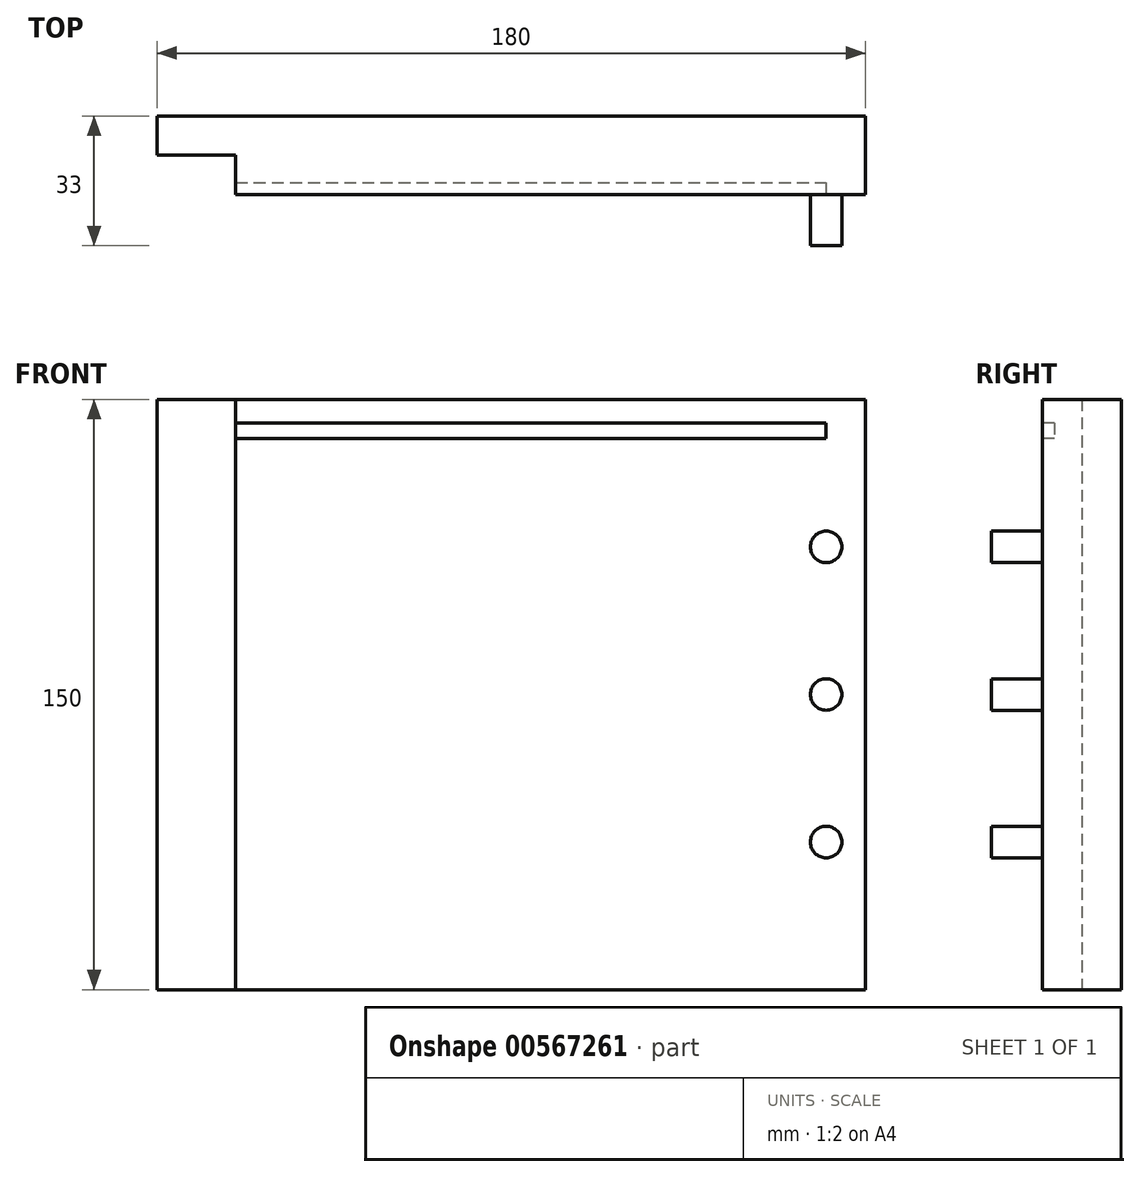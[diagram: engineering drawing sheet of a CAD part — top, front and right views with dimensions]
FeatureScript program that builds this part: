
annotation { "Feature Type Name" : "Feature", "Feature Type Description" : "" }
export const myFeature = defineFeature(function(context is Context, id is Id, definition is map)
    precondition{}
    {
        {
            var Q0;
            Q0=qCreatedBy(makeId("Front.planeOp"),FACE);
            var sketch = newSketch(context, id + "F0", { "sketchPlane" : qUnion([Q0])});
            skLineSegment(sketch, "E0.bottom", {"start": v(-86.18, 94.94) * mm, "end": v(93.82, 94.94) * mm});
            skLineSegment(sketch, "E0.top", {"start": v(-86.18, -55.06) * mm, "end": v(93.82, -55.06) * mm});
            skLineSegment(sketch, "E0.left", {"start": v(-86.18, 94.94) * mm, "end": v(-86.18, -55.06) * mm});
            skLineSegment(sketch, "E0.right", {"start": v(93.82, 94.94) * mm, "end": v(93.82, -55.06) * mm});
            skSolve(sketch);
        }
        {
            var Q0;
            Q0=makeQuery(id+"F0.imprint","IMPRINT",FACE,{"disambiguationData":[TD([[makeQuery(id+"F0.imprint","IMPRINT",EDGE,{"derivedFrom":sQuery(id+"F0.wireOp",EDGE,"E0.bottom")}),-1.0]])]});
            extrude(context, id + "F1", {"entities" : qUnion([Q0]), "depth" : 20 * mm, "offsetDistance" : 25 * mm});
        }
        {
            var Q0;
            Q0=makeQuery(id+"F1.opExtrude","CAP_FACE",FACE,{"disambiguationData":[OSD([sQuery(id+"F0.wireOp",EDGE,"E0.bottom"),sQuery(id+"F0.wireOp",EDGE,"E0.top"),sQuery(id+"F0.wireOp",EDGE,"E0.left"),sQuery(id+"F0.wireOp",EDGE,"E0.right")])],"isStart":false});
            var sketch = newSketch(context, id + "F2", { "sketchPlane" : qUnion([Q0])});
            skLineSegment(sketch, "E1", {"start": v(-66.18, 94.94) * mm, "end": v(-66.18, -55.06) * mm});
            skSolve(sketch);
        }
        {
            var Q0;
            {var subQ0=sQuery(id+"F2.wireOp",EDGE,"E1");Q0=makeQuery(id+"F2.imprint","IMPRINT",FACE,{"disambiguationData":[TD([[makeQuery(id+"F2.imprint","IMPRINT",EDGE,{"derivedFrom":subQ0}),-1.0]])]});}
            extrude(context, id + "F3", {"entities" : qUnion([Q0]), "operationType" : NewBodyOperationType.REMOVE, "oppositeDirection" : true, "depth" : 10 * mm, "offsetDistance" : 25 * mm});
        }
        {
            var Q0;
            Q0=makeQuery(id+"F1.opExtrude","CAP_FACE",FACE,{"disambiguationData":[OSD([sQuery(id+"F0.wireOp",EDGE,"E0.bottom"),sQuery(id+"F0.wireOp",EDGE,"E0.top"),sQuery(id+"F0.wireOp",EDGE,"E0.left"),sQuery(id+"F0.wireOp",EDGE,"E0.right")])],"isStart":false});
            var sketch = newSketch(context, id + "F4", { "sketchPlane" : qUnion([Q0])});
            skCircle(sketch, "E2", {"center": v(83.82, 57.44) * mm, "radius": 4 * mm});
            skLineSegment(sketch, "E3", {"start": v(73.82, 94.94) * mm, "end": v(73.82, -55.06) * mm});
            skCircle(sketch, "E4", {"center": v(83.82, -17.56) * mm, "radius": 4 * mm});
            skCircle(sketch, "E5", {"center": v(83.82, 19.94) * mm, "radius": 4 * mm});
            skSolve(sketch);
        }
        {
            var Q0;
            Q0=makeQuery(id+"F4.imprint","IMPRINT",FACE,{"disambiguationData":[TD([[makeQuery(id+"F4.imprint","IMPRINT",EDGE,{"derivedFrom":sQuery(id+"F4.wireOp",EDGE,"E2")}),1.0]])]});
            var Q1;
            Q1=makeQuery(id+"F4.imprint","IMPRINT",FACE,{"disambiguationData":[TD([[makeQuery(id+"F4.imprint","IMPRINT",EDGE,{"derivedFrom":sQuery(id+"F4.wireOp",EDGE,"E5")}),1.0]])]});
            var Q2;
            Q2=makeQuery(id+"F4.imprint","IMPRINT",FACE,{"disambiguationData":[TD([[makeQuery(id+"F4.imprint","IMPRINT",EDGE,{"derivedFrom":sQuery(id+"F4.wireOp",EDGE,"E4")}),1.0]])]});
            extrude(context, id + "F5", {"entities" : qUnion([Q0, Q1, Q2]), "operationType" : NewBodyOperationType.ADD, "depth" : 13 * mm, "offsetDistance" : 25 * mm});
        }
        {
            var Q0;
            Q0=makeQuery(id+"F1.opExtrude","CAP_FACE",FACE,{"disambiguationData":[OSD([sQuery(id+"F0.wireOp",EDGE,"E0.bottom"),sQuery(id+"F0.wireOp",EDGE,"E0.top"),sQuery(id+"F0.wireOp",EDGE,"E0.left"),sQuery(id+"F0.wireOp",EDGE,"E0.right")])],"isStart":false});
            var sketch = newSketch(context, id + "F6", { "sketchPlane" : qUnion([Q0])});
            skLineSegment(sketch, "E6", {"start": v(-66.18, 84.94) * mm, "end": v(-66.18, 88.94) * mm});
            skLineSegment(sketch, "E7", {"start": v(-66.18, 88.94) * mm, "end": v(83.82, 88.94) * mm});
            skLineSegment(sketch, "E8", {"start": v(-66.18, 84.94) * mm, "end": v(83.82, 84.94) * mm});
            skLineSegment(sketch, "E9", {"start": v(83.82, 84.94) * mm, "end": v(83.82, 88.94) * mm});
            skSolve(sketch);
        }
        {
            var Q0;
            Q0=makeQuery(id+"F6.imprint","IMPRINT",FACE,{"disambiguationData":[TD([[makeQuery(id+"F6.imprint","IMPRINT",EDGE,{"derivedFrom":sQuery(id+"F6.wireOp",EDGE,"E6")}),1.0]])]});
            extrude(context, id + "F7", {"entities" : qUnion([Q0]), "operationType" : NewBodyOperationType.REMOVE, "oppositeDirection" : true, "depth" : 3 * mm, "offsetDistance" : 25 * mm});
        }
    });
